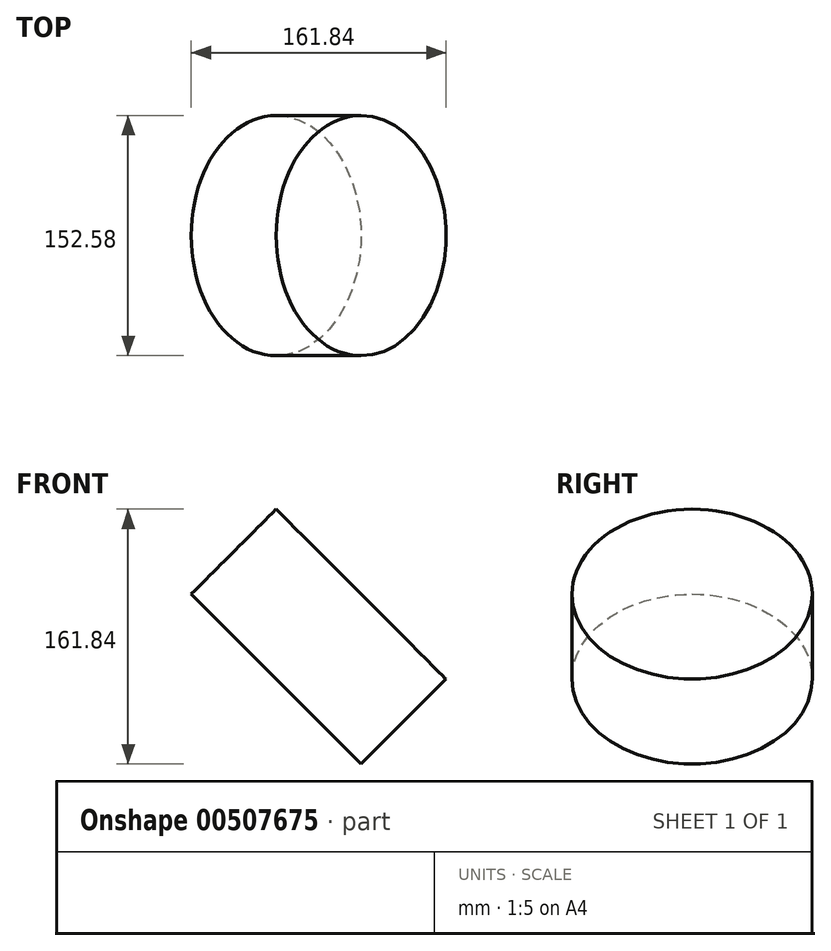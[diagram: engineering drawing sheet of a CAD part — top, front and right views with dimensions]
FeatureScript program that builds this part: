
annotation { "Feature Type Name" : "Feature", "Feature Type Description" : "" }
export const myFeature = defineFeature(function(context is Context, id is Id, definition is map)
    precondition{}
    {
        {
            var Q0;
            Q0=qCreatedBy(makeId("Front.planeOp"),FACE);
            var sketch = newSketch(context, id + "F0", { "sketchPlane" : qUnion([Q0])});
            skCircle(sketch, "E0.cCircle", {"center": v(0, 0) * mm, "radius": 53.95 * mm, "construction": true});
            skLineSegment(sketch, "E0.0", {"start": v(0, -53.95) * mm, "end": v(-53.95, 0) * mm});
            skLineSegment(sketch, "E0.1", {"start": v(-53.95, 0) * mm, "end": v(0, 53.95) * mm});
            skLineSegment(sketch, "E0.2", {"start": v(0, 53.95) * mm, "end": v(53.95, 0) * mm});
            skLineSegment(sketch, "E0.3", {"start": v(53.95, 0) * mm, "end": v(0, -53.95) * mm});
            skSolve(sketch);
        }
        {
            var Q0;
            Q0=makeQuery(id+"F0.imprint","IMPRINT",FACE,{"disambiguationData":[TD([[makeQuery(id+"F0.imprint","IMPRINT",EDGE,{"derivedFrom":sQuery(id+"F0.wireOp",EDGE,"E0.0")}),-1.0]])]});
            var Q1;
            Q1=sQuery(id+"F0.wireOp",EDGE,"E0.1");
            revolve(context, id + "F1", {"entities" : qUnion([Q0]), "axis" : qUnion([Q1]), "revolveType" : RevolveType.FULL});
        }
    });
